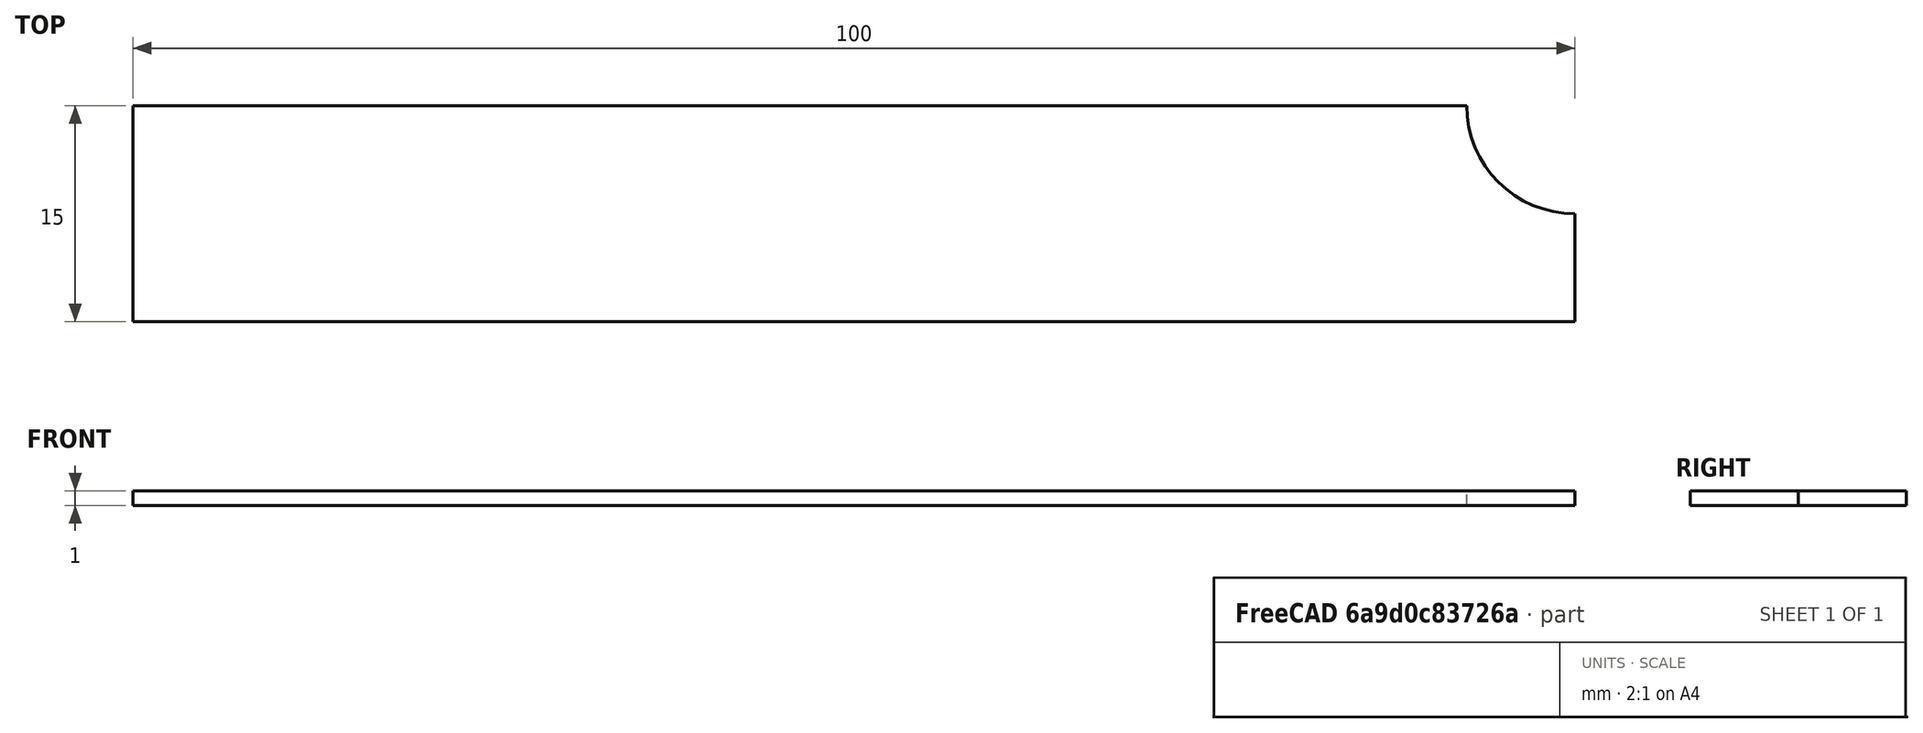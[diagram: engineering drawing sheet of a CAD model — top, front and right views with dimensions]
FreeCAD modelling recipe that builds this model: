
FCSTD DOCUMENT  (FreeCAD 0.20R29410 (Git))
Label: 1-4Model_PerforatedSpecimen(3D-model)
License: All rights reserved
LicenseURL: http://en.wikipedia.org/wiki/All_rights_reserved
objects: Sketcher::SketchObject×1, PartDesign::Pad×1, PartDesign::Body×1
note: 4 computed .brp shape members not serialized (recipe doc carries the construction recipe); baked Part::Feature solids carry a one-line shape summary decoded from their .brp

FEATURE [Sketcher::SketchObject] Sketch
  FullyConstrained = true
  MapMode = 5
  Support = -> [XY_Plane]
  sketch-geometry (5):
    g0: LineSegment StartX=-100 StartY=0 StartZ=0 EndX=-7.5 EndY=0 EndZ=0
    g1: LineSegment StartX=0 StartY=-7.5 StartZ=0 EndX=0 EndY=-15 EndZ=0
    g2: LineSegment StartX=0 StartY=-15 StartZ=0 EndX=-100 EndY=-15 EndZ=0
    g3: LineSegment StartX=-100 StartY=-15 StartZ=0 EndX=-100 EndY=0 EndZ=0
    g4: ArcOfCircle CenterX=0 CenterY=0 CenterZ=0 NormalX=0 NormalY=0 NormalZ=1 AngleXU=0 Radius=7.5 StartAngle=3.14159 EndAngle=4.71239
  constraints (15):
    c: PointOnObject(g0,g-1)
    c: PointOnObject(g0,g-1)
    c: PointOnObject(g1,g-2)
    c: PointOnObject(g1,g-2)
    c: Coincident(g1,g2)
    c: Horizontal(g2)
    c: Coincident(g2,g3)
    c: Coincident(g3,g0)
    c: Vertical(g3)
    c: Coincident(g4,g0)
    c: Coincident(g4,g1)
    c: Radius(g4) = 7.5
    c: Coincident(g-1,g4)
    c: DistanceX(g0,g1) = 100
    c: DistanceY(g1,g0) = 15
FEATURE [PartDesign::Pad] Pad
  Direction = (0,0,1)
  Length = 1
  Length2 = 10
  Profile = -> Sketch
  ReferenceAxis = -> Sketch [N_Axis]
  Type = 0
FEATURE [PartDesign::Body] Body
  Group = -> [Sketch,Pad]
  Origin = -> Origin
  Tip = -> Pad
